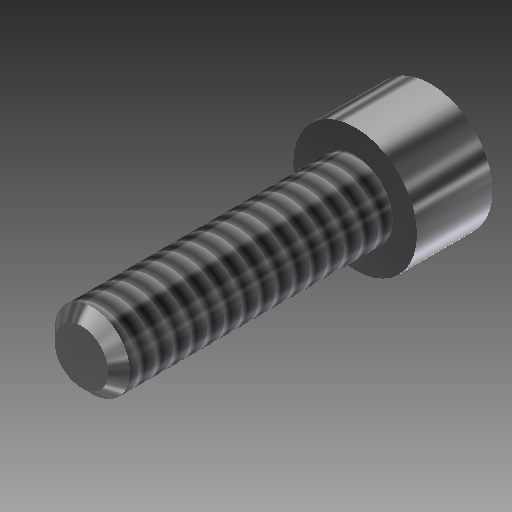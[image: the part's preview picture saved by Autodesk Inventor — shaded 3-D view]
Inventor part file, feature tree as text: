
AUTODESK INVENTOR PART (.ipt)
format: ipt  version: 2017 (Build 210142000, 142)  size: 178,176 bytes
history: native  units: in
note: dims shown in document units (in); Inventor stores cm internally (conversion verified against a paired STEP export)
features: extrude x3, sketch x3, thread x1, chamfer x1
ambient origin geometry x8: Origin, YZ Plane, XZ Plane, XY Plane, X Axis, Y Axis, Z Axis, Center Point
bodies: Solid1 (feature_tree)
feature tree (8):
  extrude  "Extrusion1"  Depth=0.5in TaperAngle=0.0deg
  extrude  "Extrusion2"  Depth=0.138in TaperAngle=0.0deg
  extrude  "Extrusion3"  Depth=0.069in TaperAngle=0.0deg
  thread  "Thread1"  [1 undecoded]
  chamfer  "Chamfer1"  Distance=0.02in Angle=45.0deg
  sketch  "Sketch1"  dims[d0=0.138in d1=0.5in d2=0.0in]
  sketch  "Sketch2"  dims[d3=0.226in d4=0.138in d5=0.0in]
  sketch  "Sketch3"  dims[d6=0.1094in d7=0.069in d8=0.0in d9=1.0in d10=0.0in d11=0.02in d12=0.125in d13=45.0deg]
note: 1 required parameter value undecoded (feature->parameter linkage not recoverable at this tier; creation-order binding heuristic only, values carry confidence <= 0.55)
